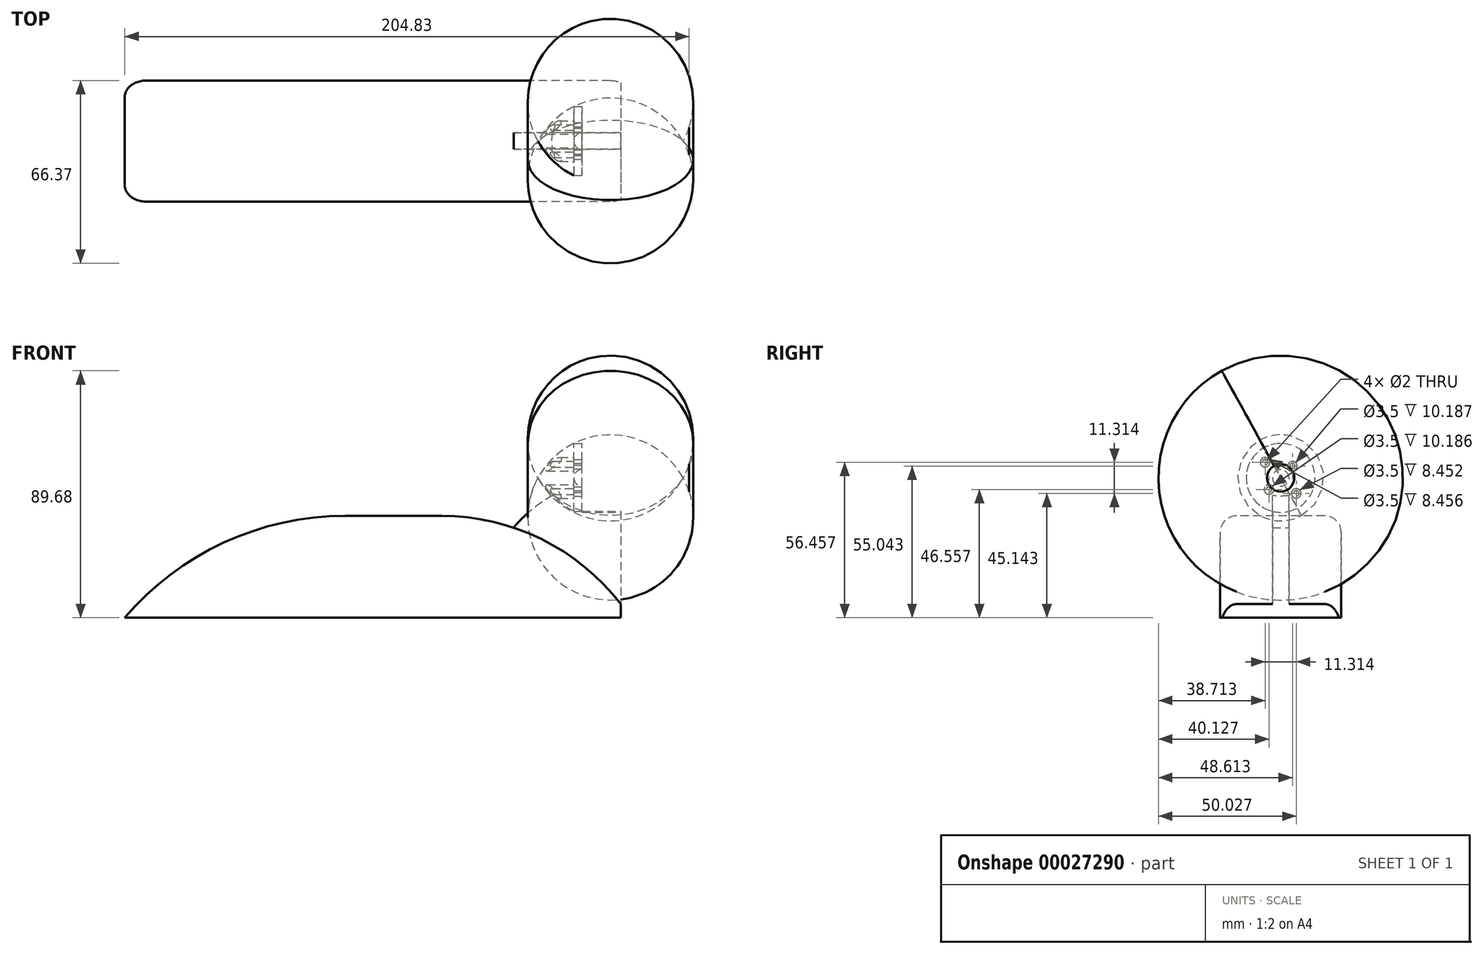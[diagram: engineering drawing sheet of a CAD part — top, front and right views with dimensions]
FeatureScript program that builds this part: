
annotation { "Feature Type Name" : "Feature", "Feature Type Description" : "" }
export const myFeature = defineFeature(function(context is Context, id is Id, definition is map)
    precondition{}
    {
        {
            var Q0;
            Q0=qCreatedBy(makeId("Top.planeOp"),FACE);
            var sketch = newSketch(context, id + "F0", { "sketchPlane" : qUnion([Q0])});
            skLineSegment(sketch, "E0.bottom", {"start": v(90, 22) * mm, "end": v(-90, 22) * mm});
            skLineSegment(sketch, "E0.top", {"start": v(90, -22) * mm, "end": v(-90, -22) * mm});
            skLineSegment(sketch, "E0.left", {"start": v(90, 22) * mm, "end": v(90, -22) * mm});
            skLineSegment(sketch, "E0.right", {"start": v(-90, 22) * mm, "end": v(-90, -22) * mm});
            skPoint(sketch, "E0.middle", {"position": v(0, 0) * mm});
            skSolve(sketch);
        }
        {
            var Q0;
            Q0=qSketchRegion(id+"F0",true);
            extrude(context, id + "F1", {"entities" : qUnion([Q0]), "depth" : 37 * mm});
        }
        {
            var Q0;
            Q0=makeQuery(id+"F1.opExtrude","SWEPT_FACE",FACE,{"disambiguationData":[OSD([sQuery(id+"F0.wireOp",EDGE,"E0.left")])]});
            var sketch = newSketch(context, id + "F2", { "sketchPlane" : qUnion([Q0])});
            skLineSegment(sketch, "E1", {"start": v(0, 0) * mm, "end": v(0, 50.8) * mm});
            skCircle(sketch, "E2", {"center": v(0, 50.8) * mm, "radius": 11.5 * mm});
            skCircle(sketch, "E3", {"center": v(0, 50.8) * mm, "radius": 50.8 * mm, "construction": true});
            skSolve(sketch);
        }
        {
            var Q0;
            Q0=qCreatedBy(makeId("Front.planeOp"),FACE);
            var sketch = newSketch(context, id + "F3", { "sketchPlane" : qUnion([Q0])});
            skLineSegment(sketch, "E4.0", {"start": v(90, 0) * mm, "end": v(90, 50.8) * mm});
            skLineSegment(sketch, "E5.0", {"start": v(-90, 37) * mm, "end": v(-90, 0) * mm});
            skLineSegment(sketch, "E6.0", {"start": v(90, 37) * mm, "end": v(-90, 37) * mm});
            skArc(sketch, "E7", {"start": v(-10, 37) * mm, "mid": v(-54.07, 27.3) * mm, "end": v(-90, 0) * mm});
            skLineSegment(sketch, "E8", {"start": v(0, 37) * mm, "end": v(0, 0) * mm, "construction": true});
            skArc(sketch, "E9", {"start": v(90, 5) * mm, "mid": v(61.22, 28.57) * mm, "end": v(25, 37) * mm});
            skSolve(sketch);
        }
        {
            var Q0;
            Q0=qSketchRegion(id+"F3",true);
            extrude(context, id + "F4", {"entities" : qUnion([Q0]), "operationType" : NewBodyOperationType.REMOVE, "oppositeDirection" : true, "depth" : 25 * mm, "hasSecondDirection" : true, "secondDirectionOppositeDirection" : false, "secondDirectionDepth" : 25 * mm});
        }
        {
            var Q0;
            Q0=qCreatedBy(makeId("Front.planeOp"),FACE);
            var sketch = newSketch(context, id + "F5", { "sketchPlane" : qUnion([Q0])});
            skLineSegment(sketch, "E10.top", {"start": v(48, 32) * mm, "end": v(-32, 32) * mm});
            skLineSegment(sketch, "E10.right", {"start": v(-32, 2) * mm, "end": v(-32, 32) * mm});
            skLineSegment(sketch, "E11", {"start": v(48, 32) * mm, "end": v(48, 2) * mm});
            skLineSegment(sketch, "E12", {"start": v(48, 2) * mm, "end": v(-32, 2) * mm});
            skSolve(sketch);
        }
        {
            var Q0;
            Q0=qSketchRegion(id+"F5",true);
            extrude(context, id + "F6", {"entities" : qUnion([Q0]), "depth" : (35 / 2) * mm, "hasSecondDirection" : true, "secondDirectionOppositeDirection" : true, "secondDirectionDepth" : 17.5 * mm});
        }
        {
            var Q0;
            Q0=makeQuery(id+"F4.boolean.opBoolean","INTERSECT",EDGE,{"derivedFrom":[makeQuery(id+"F1.opExtrude","SWEPT_FACE",FACE,{"disambiguationData":[OSD([sQuery(id+"F0.wireOp",EDGE,"E0.bottom")])]}),makeQuery(id+"F4.opExtrude","SWEPT_FACE",FACE,{"disambiguationData":[OSD([sQuery(id+"F3.wireOp",EDGE,"E7")])]})]});
            var Q1;
            Q1=makeQuery(id+"F1.opExtrude","CAP_EDGE",EDGE,{"disambiguationData":[OSD([sQuery(id+"F0.wireOp",EDGE,"E0.bottom")])],"isStart":false});
            var Q2;
            Q2=makeQuery(id+"F4.boolean.opBoolean","INTERSECT",EDGE,{"derivedFrom":[makeQuery(id+"F1.opExtrude","SWEPT_FACE",FACE,{"disambiguationData":[OSD([sQuery(id+"F0.wireOp",EDGE,"E0.top")])]}),makeQuery(id+"F4.opExtrude","SWEPT_FACE",FACE,{"disambiguationData":[OSD([sQuery(id+"F3.wireOp",EDGE,"E7")])]})]});
            var Q3;
            Q3=makeQuery(id+"F4.boolean.opBoolean","INTERSECT",EDGE,{"derivedFrom":[makeQuery(id+"F1.opExtrude","SWEPT_FACE",FACE,{"disambiguationData":[OSD([sQuery(id+"F0.wireOp",EDGE,"E0.bottom")])]}),makeQuery(id+"F4.opExtrude","SWEPT_FACE",FACE,{"disambiguationData":[OSD([sQuery(id+"F3.wireOp",EDGE,"E9")])]})]});
            fillet(context, id + "F7", {"entities" : qUnion([Q0, Q1, Q2, Q3]), "radius" : 6 * mm, "tangentPropagation" : true, "allowEdgeOverflow" : false});
        }
        {
            var Q0;
            {var subQ1=sQuery(id+"F0.wireOp",EDGE,"E0.left");var subQ6=makeQuery(id+"F1.opExtrude","SWEPT_EDGE",EDGE,{"disambiguationData":[OSD([sQuery(id+"F0.wireOp",EDGE,"E0.top"),subQ1])]});Q0=makeQuery(id+"F2.imprint","IMPRINT",FACE,{"disambiguationData":[TD([[makeQuery(id+"F2.imprint","IMPRINT",EDGE,{"derivedFrom":subQ6}),1.0]])]});}
            var sketch = newSketch(context, id + "F8", { "sketchPlane" : qUnion([Q0])});
            skLineSegment(sketch, "E13.bottom", {"start": v(-3, 50.8) * mm, "end": v(3, 50.8) * mm});
            skLineSegment(sketch, "E13.top", {"start": v(-3, 0) * mm, "end": v(3, 0) * mm});
            skLineSegment(sketch, "E13.left", {"start": v(-3, 50.8) * mm, "end": v(-3, 0) * mm});
            skLineSegment(sketch, "E13.right", {"start": v(3, 50.8) * mm, "end": v(3, 0) * mm});
            skPoint(sketch, "E13.middle", {"position": v(0, 25.4) * mm});
            skLineSegment(sketch, "E14.0", {"start": v(0, 0) * mm, "end": v(0, 50.8) * mm, "construction": true});
            skSolve(sketch);
        }
        {
            var Q0;
            Q0=qSketchRegion(id+"F8",true);
            var Q1;
            Q1=sQuery(id+"F8.wireOp",EDGE,"E13.top");
            revolve(context, id + "F9", {"operationType" : NewBodyOperationType.ADD, "entities" : qUnion([Q0]), "axis" : qUnion([Q1]), "revolveType" : RevolveType.ONE_DIRECTION, "oppositeDirection" : true, "angle" : 56 * degree});
        }
        {
            var Q0;
            Q0=makeQuery(id+"F2.imprint","IMPRINT",FACE,{"disambiguationData":[TD([[makeQuery(id+"F2.imprint","IMPRINT",EDGE,{"derivedFrom":sQuery(id+"F2.wireOp",EDGE,"E2")}),1.0]])]});
            var sketch = newSketch(context, id + "F10", { "sketchPlane" : qUnion([Q0])});
            skCircle(sketch, "E15.0", {"center": v(0, 50.8) * mm, "radius": 11.5 * mm, "construction": true});
            skCircle(sketch, "E16.0", {"center": v(0, 50.8) * mm, "radius": 12.5 * mm});
            skSolve(sketch);
        }
        {
            var Q0;
            Q0=qSketchRegion(id+"F10",true);
            extrude(context, id + "F11", {"entities" : qUnion([Q0]), "operationType" : NewBodyOperationType.REMOVE, "oppositeDirection" : true, "depth" : 14 * mm});
        }
        {
            var Q0;
            Q0=qCreatedBy(makeId("Front.planeOp"),FACE);
            var sketch = newSketch(context, id + "F12", { "sketchPlane" : qUnion([Q0])});
            skPoint(sketch, "E17.0", {"position": v(90, 50.8) * mm});
            skLineSegment(sketch, "E18", {"start": v(90, 50.8) * mm, "end": v(60, 50.8) * mm});
            skLineSegment(sketch, "E19", {"start": v(73, 50.8) * mm, "end": v(73, 38.3) * mm, "construction": true});
            skArc(sketch, "E20", {"start": v(60, 50.8) * mm, "mid": v(65.54, 43.55) * mm, "end": v(73, 38.3) * mm});
            skLineSegment(sketch, "E21.0", {"start": v(76, 38.3) * mm, "end": v(76, 50.8) * mm});
            skPoint(sketch, "E22.orphan", {"position": v(76, 48.83) * mm});
            skLineSegment(sketch, "E23", {"start": v(73, 38.3) * mm, "end": v(76, 38.3) * mm});
            skPoint(sketch, "E24.orphan", {"position": v(76, 38.67) * mm});
            skSolve(sketch);
        }
        {
            var Q0;
            Q0=qSketchRegion(id+"F12",true);
            var Q1;
            Q1=sQuery(id+"F12.wireOp",EDGE,"E18");
            revolve(context, id + "F13", {"operationType" : NewBodyOperationType.ADD, "entities" : qUnion([Q0]), "axis" : qUnion([Q1]), "revolveType" : RevolveType.FULL});
        }
        {
            var Q0;
            Q0=makeQuery(id+"F13.boolean.opBoolean","MERGE",FACE,{"derivedFrom":[makeQuery(id+"F11.boolean.opBoolean","COPY",FACE,{"derivedFrom":makeQuery(id+"F11.opExtrude","CAP_FACE",FACE,{"disambiguationData":[OSD([sQuery(id+"F10.wireOp",EDGE,"E16.0")])],"isStart":false})}),makeQuery(id+"F13.opRevolve","SWEPT_FACE",FACE,{"disambiguationData":[OSD([sQuery(id+"F12.wireOp",EDGE,"E21.0")])]})]});
            var sketch = newSketch(context, id + "F14", { "sketchPlane" : qUnion([Q0])});
            skLineSegment(sketch, "E25", {"start": v(5.66, 45.14) * mm, "end": v(-5.66, 56.46) * mm, "construction": true});
            skLineSegment(sketch, "E26", {"start": v(4.24, 55.04) * mm, "end": v(-4.24, 46.56) * mm, "construction": true});
            skCircle(sketch, "E27", {"center": v(-5.66, 56.46) * mm, "radius": 1 * mm});
            skCircle(sketch, "E28", {"center": v(4.24, 55.04) * mm, "radius": 1 * mm});
            skCircle(sketch, "E29", {"center": v(-4.24, 46.56) * mm, "radius": 1 * mm});
            skCircle(sketch, "E30", {"center": v(5.66, 45.14) * mm, "radius": 1 * mm});
            skSolve(sketch);
        }
        {
            var Q0;
            Q0=qSketchRegion(id+"F14",true);
            extrude(context, id + "F15", {"entities" : qUnion([Q0]), "operationType" : NewBodyOperationType.REMOVE, "endBound" : BoundingType.THROUGH_ALL, "oppositeDirection" : true, "depth" : 25 * mm});
        }
        {
            var Q0;
            Q0=makeQuery(id+"F13.boolean.opBoolean","MERGE",FACE,{"derivedFrom":[makeQuery(id+"F11.boolean.opBoolean","COPY",FACE,{"derivedFrom":makeQuery(id+"F11.opExtrude","CAP_FACE",FACE,{"disambiguationData":[OSD([sQuery(id+"F10.wireOp",EDGE,"E16.0")])],"isStart":false})}),makeQuery(id+"F13.opRevolve","SWEPT_FACE",FACE,{"disambiguationData":[OSD([sQuery(id+"F12.wireOp",EDGE,"E21.0")])]})]});
            var sketch = newSketch(context, id + "F16", { "sketchPlane" : qUnion([Q0])});
            skCircle(sketch, "E31", {"center": v(0, 50.8) * mm, "radius": 3 * mm});
            skSolve(sketch);
        }
        {
            var Q0;
            Q0=qSketchRegion(id+"F16",true);
            extrude(context, id + "F17", {"entities" : qUnion([Q0]), "operationType" : NewBodyOperationType.REMOVE, "oppositeDirection" : true, "depth" : 3 * mm});
        }
        {
            var Q0;
            Q0=makeQuery(id+"F17.boolean.opBoolean","COPY",EDGE,{"derivedFrom":makeQuery(id+"F17.opExtrude","CAP_EDGE",EDGE,{"disambiguationData":[OSD([sQuery(id+"F16.wireOp",EDGE,"E31")])],"isStart":false})});
            fillet(context, id + "F18", {"entities" : qUnion([Q0]), "radius" : 3 * mm, "tangentPropagation" : true, "allowEdgeOverflow" : false});
        }
        {
            var Q0;
            Q0=makeQuery(id+"F13.boolean.opBoolean","MERGE",FACE,{"derivedFrom":[makeQuery(id+"F11.boolean.opBoolean","COPY",FACE,{"derivedFrom":makeQuery(id+"F11.opExtrude","CAP_FACE",FACE,{"disambiguationData":[OSD([sQuery(id+"F10.wireOp",EDGE,"E16.0")])],"isStart":false})}),makeQuery(id+"F13.opRevolve","SWEPT_FACE",FACE,{"disambiguationData":[OSD([sQuery(id+"F12.wireOp",EDGE,"E21.0")])]})]});
            var sketch = newSketch(context, id + "F19", { "sketchPlane" : qUnion([Q0])});
            skCircle(sketch, "E32", {"center": v(-5.66, 56.46) * mm, "radius": 1.75 * mm});
            skCircle(sketch, "E33", {"center": v(4.24, 55.04) * mm, "radius": 1.75 * mm});
            skCircle(sketch, "E34", {"center": v(5.66, 45.14) * mm, "radius": 1.75 * mm});
            skCircle(sketch, "E35", {"center": v(-4.24, 46.56) * mm, "radius": 1.75 * mm});
            skSolve(sketch);
        }
        {
            var Q0;
            Q0=qSketchRegion(id+"F19",true);
            extrude(context, id + "F20", {"entities" : qUnion([Q0]), "operationType" : NewBodyOperationType.REMOVE, "endBound" : BoundingType.THROUGH_ALL, "oppositeDirection" : true, "depth" : 6.3 * mm, "hasSecondDirection" : true, "secondDirectionOppositeDirection" : true, "secondDirectionDepth" : 3 * mm});
        }
    });
